# Revit family: PGR_Noken_SntryAppIncTrps_Sifon
name_source: partatom
category: Plumbing Fixtures
revit_build: Autodesk Revit 2017 (Build: 20171027_0315(x64)
units: mm (PartAtom-declared; Revit-internal decimal feet)

## family parameters
Always vertical = Yes
Cut with Voids When Loaded = No
Host = Wall
OmniClass Number = 23.45.55.11
OmniClass Title = Sanitary Components
Part Type = Normal
Room Calculation Point = No
Round Connector Dimension = Use Diameter
Shared = Yes

## types (1)
- Sifon-100039181
    AccessibilityPerformance = SeeProductInformation for technical PDF
    ApplicationType = Basin
    AssetType = Fixed
    BIMObjectName = PGR_Noken_SanitaryApplianceTraps_Complementos_White-345x70x255mm-100039181
    Category = Pr_65_52_25_75: Sanitary appliance traps.
    CodePerformance = EN 274, EN 248
    Collection = Complementos
    Color = Chrome
    Description = Bottle trap. Material brass, finish chrome plated, nominal length 345 mm, nominal width 70 mm, nominal height 165-255 mm, net product weight 0,5 kg . Normative UNE EN 274, EN 248
    DrainSize = 40 mm
    DurationUnit = Year
    Features = See ProductInformation for technical PDF
    Finish = Chrome plated
    Height = 550 mm
    HeightTrap = 220 mm  [stored 0.721785 ft]
    IfcExportAs = IfcWasteTerminalType
    IfcExportType = WasteTrap
    ManufacturerURL = www.noken.com
    Material = Brass
    MaterialMetal = PGR_Noken_Brass_Chrome
    Model = 100039181
    ModelNumber = 100039181
    ModelReference = SIFON BOTELLA 300 CROMO
    NBSDescription = Sanitary appliance traps
    NBSReference = 90-10-60/410
    Name = SanitaryApplianceTraps_Complementos_White-345x70x255mm-100039181
    NettWeight = 5
    NominalHeight = 220 mm  [stored 0.721785 ft]
    NominalHeightRange = 165-255
    NominalWidth = 70 mm  [stored 0.229659 ft]
    NumberOfConnections = 2
    ProductInformation = http://calidad.info-grupo.com:8081
    Reference = -
    Size = 345x70x255mm
    Status = UNSET
    SustainabilityPerformance = See ProductInformation for technical PDF
    TechnicalDrawing = See ProductInformation for technical PDF
    Type Image = <None>
    URL = www.noken.com
    Uniclass2015Code = Pr_65_52_25_75
    Uniclass2015Title = Sanitary appliance traps
    Uniclass2015Version = V1_9
    Version = 1
    WFU = 0
    WarrantyDescription = See ProductInformation for technical PDF
    WarrantyDurationUnit = year
    WasteTrapType = UNSET

note: [stored X ft] marks values corroborated as IEEE doubles in the binary element streams (Revit-internal decimal feet)

## geometry (parser evidence)
native form markers: Blend x2, Sweep x6
no freeform markers — native parametric forms only
